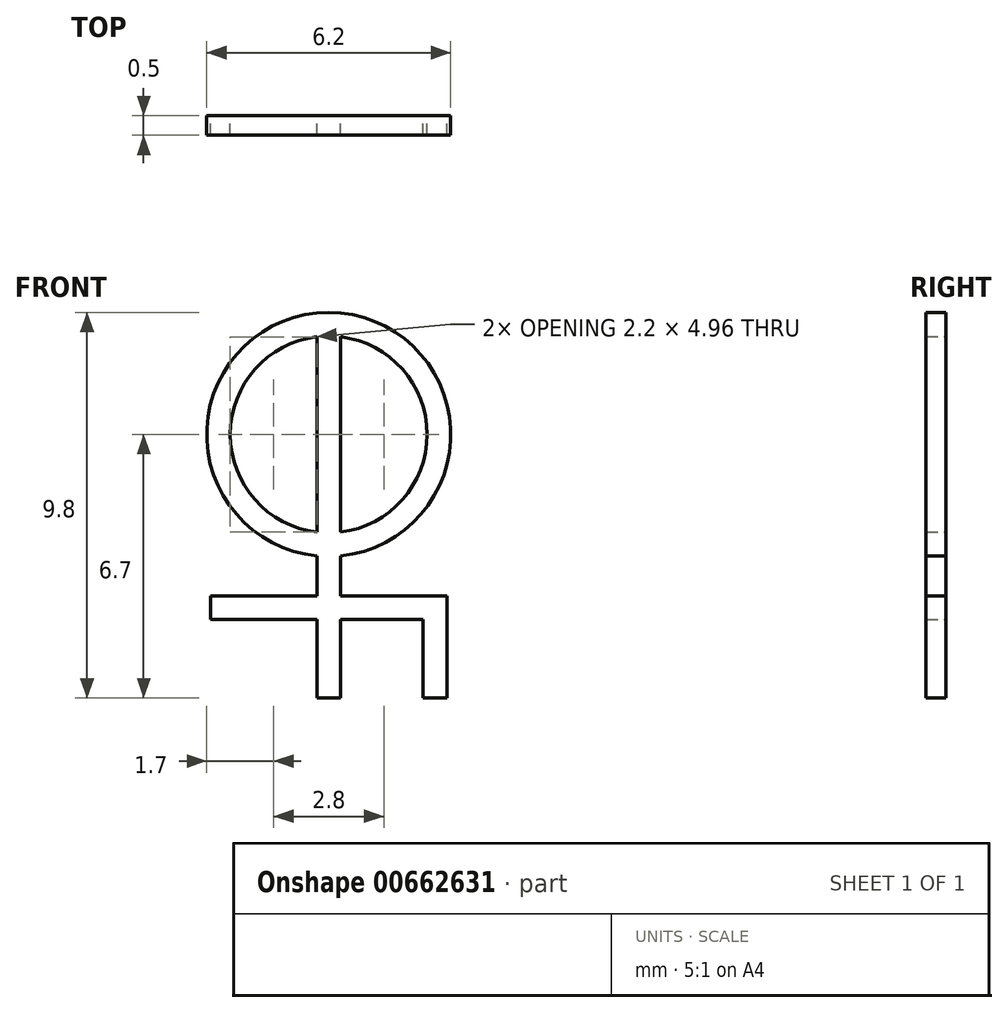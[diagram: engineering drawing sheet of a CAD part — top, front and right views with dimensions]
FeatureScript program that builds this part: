
annotation { "Feature Type Name" : "Feature", "Feature Type Description" : "" }
export const myFeature = defineFeature(function(context is Context, id is Id, definition is map)
    precondition{}
    {
        {
            var Q0;
            Q0=qCreatedBy(makeId("Front.planeOp"),FACE);
            var sketch = newSketch(context, id + "F0", { "sketchPlane" : qUnion([Q0])});
            skArc(sketch, "E0", {"start": v(0.3, -2.48) * mm, "mid": v(2.5, 0) * mm, "end": v(0.3, 2.48) * mm});
            skArc(sketch, "E1.0", {"start": v(0.3, -3.09) * mm, "mid": v(0, 3.1) * mm, "end": v(-0.3, -3.09) * mm});
            skLineSegment(sketch, "E2", {"start": v(-0.3, 2.48) * mm, "end": v(-0.3, -2.48) * mm});
            skLineSegment(sketch, "E3", {"start": v(0.3, 2.48) * mm, "end": v(0.3, -2.48) * mm});
            skLineSegment(sketch, "E4", {"start": v(0.3, -6.7) * mm, "end": v(-0.3, -6.7) * mm});
            skLineSegment(sketch, "E5", {"start": v(-3, -4.1) * mm, "end": v(-0.3, -4.1) * mm});
            skLineSegment(sketch, "E6", {"start": v(3, -4.1) * mm, "end": v(3, -6.7) * mm});
            skLineSegment(sketch, "E7", {"start": v(3, -6.7) * mm, "end": v(2.4, -6.7) * mm});
            skLineSegment(sketch, "E8", {"start": v(2.4, -6.7) * mm, "end": v(2.4, -4.7) * mm});
            skLineSegment(sketch, "E9", {"start": v(2.4, -4.7) * mm, "end": v(0.3, -4.7) * mm});
            skLineSegment(sketch, "E10", {"start": v(-3, -4.1) * mm, "end": v(-3, -4.7) * mm});
            skArc(sketch, "E11.trimOffspring", {"start": v(-0.3, 2.48) * mm, "mid": v(-2.5, 0) * mm, "end": v(-0.3, -2.48) * mm});
            skLineSegment(sketch, "E12.trimOffspring", {"start": v(-0.3, -3.09) * mm, "end": v(-0.3, -4.1) * mm});
            skLineSegment(sketch, "E13.trimOffspring", {"start": v(0.3, -3.09) * mm, "end": v(0.3, -4.1) * mm});
            skLineSegment(sketch, "E14.trimOffspring", {"start": v(-0.3, -4.7) * mm, "end": v(-0.3, -6.7) * mm});
            skLineSegment(sketch, "E15.trimOffspring", {"start": v(0.3, -4.1) * mm, "end": v(3, -4.1) * mm});
            skLineSegment(sketch, "E16.trimOffspring", {"start": v(0.3, -4.7) * mm, "end": v(0.3, -6.7) * mm});
            skLineSegment(sketch, "E17.trimOffspring", {"start": v(-0.3, -4.7) * mm, "end": v(-3, -4.7) * mm});
            skSolve(sketch);
        }
        {
            var Q0;
            Q0=makeQuery(id+"F0.imprint","IMPRINT",FACE,{"disambiguationData":[TD([[makeQuery(id+"F0.imprint","IMPRINT",EDGE,{"derivedFrom":sQuery(id+"F0.wireOp",EDGE,"E0")}),-1.0]])]});
            extrude(context, id + "F1", {"entities" : qUnion([Q0]), "depth" : .5 * mm, "offsetDistance" : 25 * mm});
        }
    });
